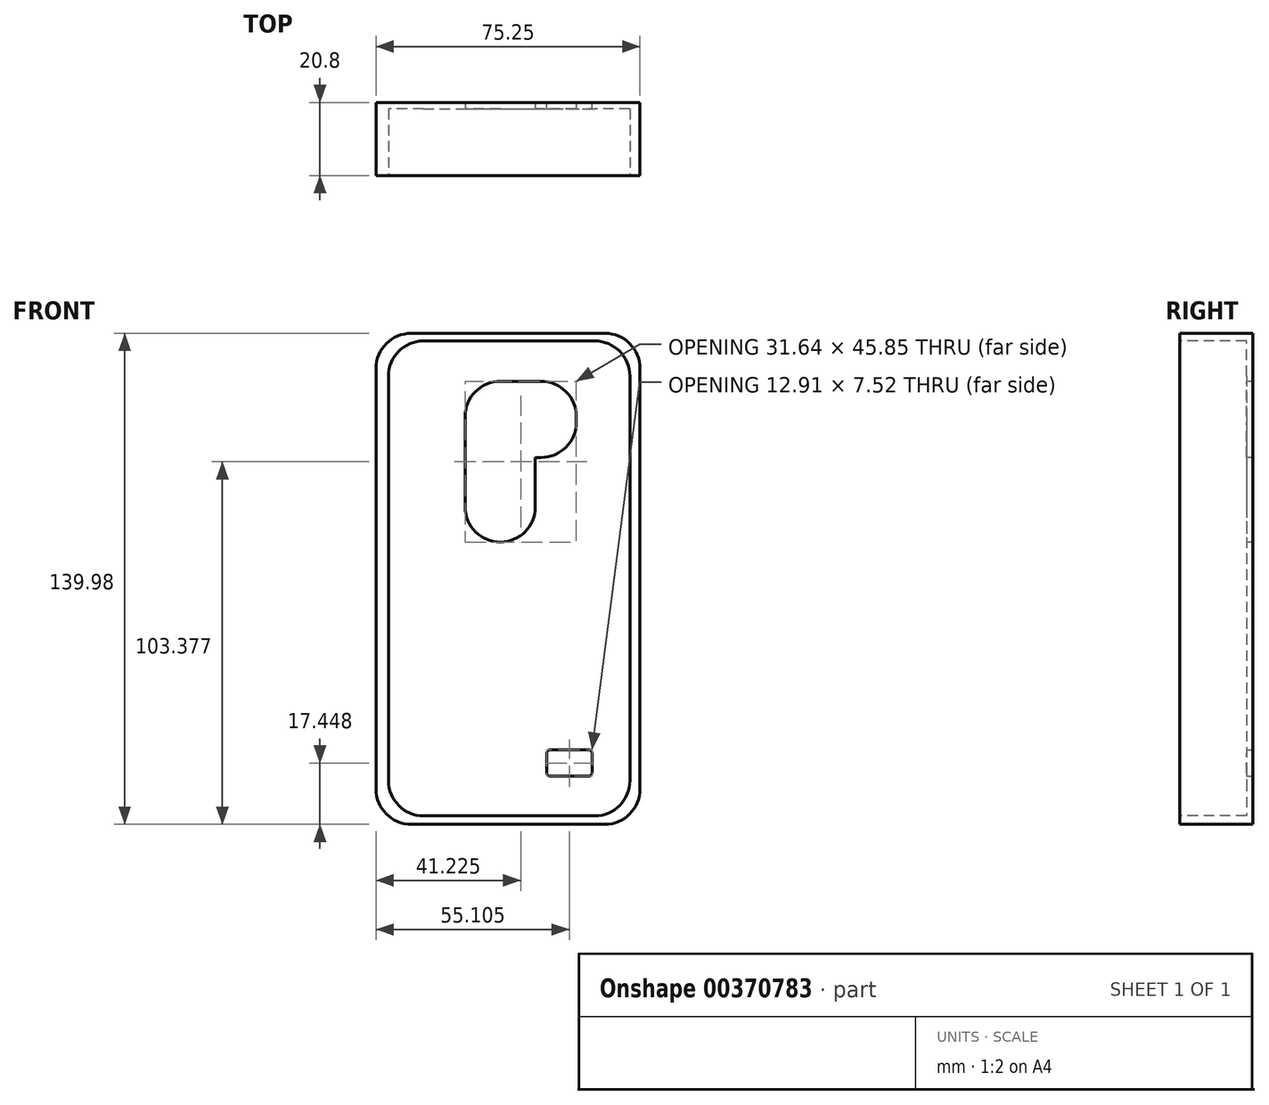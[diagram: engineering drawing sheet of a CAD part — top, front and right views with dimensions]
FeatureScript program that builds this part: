
annotation { "Feature Type Name" : "Feature", "Feature Type Description" : "" }
export const myFeature = defineFeature(function(context is Context, id is Id, definition is map)
    precondition{}
    {
        {
            var Q0;
            Q0=qCreatedBy(makeId("Front.planeOp"),FACE);
            var sketch = newSketch(context, id + "F0", { "sketchPlane" : qUnion([Q0])});
            skLineSegment(sketch, "E0.bottom", {"start": v(-27.78, 71) * mm, "end": v(27.47, 71) * mm});
            skLineSegment(sketch, "E0.top", {"start": v(-27.78, -68.98) * mm, "end": v(27.47, -68.98) * mm});
            skLineSegment(sketch, "E0.left", {"start": v(-37.78, 61) * mm, "end": v(-37.78, -58.98) * mm});
            skLineSegment(sketch, "E0.right", {"start": v(37.47, 61) * mm, "end": v(37.47, -58.98) * mm});
            skPoint(sketch, "E1.visualSharp", {"position": v(-37.78, 71) * mm});
            skArc(sketch, "E1.filletArc", {"start": v(-27.78, 71) * mm, "mid": v(-34.85, 68.07) * mm, "end": v(-37.78, 61) * mm});
            skPoint(sketch, "E2.visualSharp", {"position": v(37.47, 71) * mm});
            skArc(sketch, "E2.filletArc", {"start": v(37.47, 61) * mm, "mid": v(34.54, 68.07) * mm, "end": v(27.47, 71) * mm});
            skPoint(sketch, "E3.visualSharp", {"position": v(37.47, -68.98) * mm});
            skArc(sketch, "E3.filletArc", {"start": v(27.47, -68.98) * mm, "mid": v(34.54, -66.05) * mm, "end": v(37.47, -58.98) * mm});
            skPoint(sketch, "E4.visualSharp", {"position": v(-37.78, -68.98) * mm});
            skArc(sketch, "E4.filletArc", {"start": v(-37.78, -58.98) * mm, "mid": v(-34.85, -66.05) * mm, "end": v(-27.78, -68.98) * mm});
            skSolve(sketch);
        }
        {
            var Q0;
            Q0=makeQuery(id+"F0.imprint","IMPRINT",FACE,{"disambiguationData":[TD([[makeQuery(id+"F0.imprint","IMPRINT",EDGE,{"derivedFrom":sQuery(id+"F0.wireOp",EDGE,"E0.bottom")}),-1.0]])]});
            extrude(context, id + "F1", {"entities" : qUnion([Q0]), "depth" : 20.8 * mm});
        }
        {
            var Q0;
            Q0=makeQuery(id+"F1.opExtrude","CAP_FACE",FACE,{"disambiguationData":[OSD([sQuery(id+"F0.wireOp",EDGE,"E0.bottom"),sQuery(id+"F0.wireOp",EDGE,"E0.top"),sQuery(id+"F0.wireOp",EDGE,"E0.left"),sQuery(id+"F0.wireOp",EDGE,"E0.right"),sQuery(id+"F0.wireOp",EDGE,"E1.filletArc"),sQuery(id+"F0.wireOp",EDGE,"E2.filletArc"),sQuery(id+"F0.wireOp",EDGE,"E3.filletArc"),sQuery(id+"F0.wireOp",EDGE,"E4.filletArc")])],"isStart":false});
            var sketch = newSketch(context, id + "F2", { "sketchPlane" : qUnion([Q0])});
            skLineSegment(sketch, "E5.bottom", {"start": v(-24.27, 68.82) * mm, "end": v(24.58, 68.82) * mm});
            skLineSegment(sketch, "E5.top", {"start": v(-24.27, -66.56) * mm, "end": v(24.58, -66.56) * mm});
            skLineSegment(sketch, "E5.left", {"start": v(-34.27, 58.82) * mm, "end": v(-34.27, -56.56) * mm});
            skLineSegment(sketch, "E5.right", {"start": v(34.58, 58.82) * mm, "end": v(34.58, -56.56) * mm});
            skPoint(sketch, "E6.visualSharp", {"position": v(-34.27, 68.82) * mm});
            skArc(sketch, "E6.filletArc", {"start": v(-24.27, 68.82) * mm, "mid": v(-31.34, 65.9) * mm, "end": v(-34.27, 58.82) * mm});
            skPoint(sketch, "E7.visualSharp", {"position": v(34.58, 68.82) * mm});
            skArc(sketch, "E7.filletArc", {"start": v(34.58, 58.82) * mm, "mid": v(31.65, 65.9) * mm, "end": v(24.58, 68.82) * mm});
            skPoint(sketch, "E8.visualSharp", {"position": v(34.58, -66.56) * mm});
            skArc(sketch, "E8.filletArc", {"start": v(24.58, -66.56) * mm, "mid": v(31.65, -63.64) * mm, "end": v(34.58, -56.56) * mm});
            skPoint(sketch, "E9.visualSharp", {"position": v(-34.27, -66.56) * mm});
            skArc(sketch, "E9.filletArc", {"start": v(-34.27, -56.56) * mm, "mid": v(-31.34, -63.64) * mm, "end": v(-24.27, -66.56) * mm});
            skSolve(sketch);
        }
        {
            var Q0;
            Q0=makeQuery(id+"F2.imprint","IMPRINT",FACE,{"disambiguationData":[TD([[makeQuery(id+"F2.imprint","IMPRINT",EDGE,{"derivedFrom":sQuery(id+"F2.wireOp",EDGE,"E5.bottom")}),-1.0]])]});
            extrude(context, id + "F3", {"entities" : qUnion([Q0]), "operationType" : NewBodyOperationType.REMOVE, "oppositeDirection" : true, "depth" : 19 * mm});
        }
        {
            var Q0;
            Q0=makeQuery(id+"F3.boolean.opBoolean","COPY",FACE,{"derivedFrom":makeQuery(id+"F3.opExtrude","CAP_FACE",FACE,{"disambiguationData":[OSD([sQuery(id+"F2.wireOp",EDGE,"E5.bottom"),sQuery(id+"F2.wireOp",EDGE,"E5.top"),sQuery(id+"F2.wireOp",EDGE,"E5.left"),sQuery(id+"F2.wireOp",EDGE,"E5.right"),sQuery(id+"F2.wireOp",EDGE,"E6.filletArc"),sQuery(id+"F2.wireOp",EDGE,"E7.filletArc"),sQuery(id+"F2.wireOp",EDGE,"E8.filletArc"),sQuery(id+"F2.wireOp",EDGE,"E9.filletArc")])],"isStart":false})});
            var sketch = newSketch(context, id + "F4", { "sketchPlane" : qUnion([Q0])});
            skLineSegment(sketch, "E10.bottom", {"start": v(-2.37, 57.32) * mm, "end": v(9.27, 57.32) * mm});
            skLineSegment(sketch, "E10.left", {"start": v(-12.37, 47.32) * mm, "end": v(-12.37, 21.47) * mm});
            skLineSegment(sketch, "E11", {"start": v(9.27, 35.57) * mm, "end": v(7.63, 35.57) * mm});
            skLineSegment(sketch, "E12", {"start": v(7.63, 35.57) * mm, "end": v(7.63, 21.47) * mm});
            skLineSegment(sketch, "E13", {"start": v(19.27, 47.32) * mm, "end": v(19.27, 45.57) * mm});
            skLineSegment(sketch, "E14", {"start": v(-2.37, 11.47) * mm, "end": v(-2.37, 11.47) * mm});
            skPoint(sketch, "E15.visualSharp", {"position": v(19.27, 35.57) * mm});
            skArc(sketch, "E15.filletArc", {"start": v(9.27, 35.57) * mm, "mid": v(16.34, 38.5) * mm, "end": v(19.27, 45.57) * mm});
            skPoint(sketch, "E16.visualSharp", {"position": v(19.27, 57.32) * mm});
            skArc(sketch, "E16.filletArc", {"start": v(19.27, 47.32) * mm, "mid": v(16.34, 54.4) * mm, "end": v(9.27, 57.32) * mm});
            skPoint(sketch, "E17.visualSharp", {"position": v(-12.37, 57.32) * mm});
            skArc(sketch, "E17.filletArc", {"start": v(-2.37, 57.32) * mm, "mid": v(-9.45, 54.4) * mm, "end": v(-12.37, 47.32) * mm});
            skPoint(sketch, "E18.visualSharp", {"position": v(-12.37, 11.47) * mm});
            skArc(sketch, "E18.filletArc", {"start": v(-12.37, 21.47) * mm, "mid": v(-9.45, 14.4) * mm, "end": v(-2.37, 11.47) * mm});
            skPoint(sketch, "E19.visualSharp", {"position": v(7.63, 11.47) * mm});
            skArc(sketch, "E19.filletArc", {"start": v(-2.37, 11.47) * mm, "mid": v(4.7, 14.4) * mm, "end": v(7.63, 21.47) * mm});
            skSolve(sketch);
        }
        {
            var Q0;
            Q0=makeQuery(id+"F4.imprint","IMPRINT",FACE,{"disambiguationData":[TD([[makeQuery(id+"F4.imprint","IMPRINT",EDGE,{"derivedFrom":sQuery(id+"F4.wireOp",EDGE,"E10.bottom")}),-1.0]])]});
            extrude(context, id + "F5", {"entities" : qUnion([Q0]), "operationType" : NewBodyOperationType.REMOVE, "oppositeDirection" : true, "depth" : 25 * mm});
        }
        {
            var Q0;
            Q0=makeQuery(id+"F1.opExtrude","CAP_FACE",FACE,{"disambiguationData":[OSD([sQuery(id+"F0.wireOp",EDGE,"E0.bottom"),sQuery(id+"F0.wireOp",EDGE,"E0.top"),sQuery(id+"F0.wireOp",EDGE,"E0.left"),sQuery(id+"F0.wireOp",EDGE,"E0.right"),sQuery(id+"F0.wireOp",EDGE,"E1.filletArc"),sQuery(id+"F0.wireOp",EDGE,"E2.filletArc"),sQuery(id+"F0.wireOp",EDGE,"E3.filletArc"),sQuery(id+"F0.wireOp",EDGE,"E4.filletArc")])],"isStart":true});
            var sketch = newSketch(context, id + "F6", { "sketchPlane" : qUnion([Q0])});
            skLineSegment(sketch, "E20.bottom", {"start": v(-22.78, -47.77) * mm, "end": v(-11.87, -47.77) * mm});
            skLineSegment(sketch, "E20.top", {"start": v(-22.78, -55.3) * mm, "end": v(-11.87, -55.3) * mm});
            skLineSegment(sketch, "E20.left", {"start": v(-23.78, -48.77) * mm, "end": v(-23.78, -54.3) * mm});
            skLineSegment(sketch, "E20.right", {"start": v(-10.87, -48.77) * mm, "end": v(-10.87, -54.3) * mm});
            skPoint(sketch, "E21.visualSharp", {"position": v(-23.78, -47.77) * mm});
            skArc(sketch, "E21.filletArc", {"start": v(-22.78, -47.77) * mm, "mid": v(-23.49, -48.07) * mm, "end": v(-23.78, -48.77) * mm});
            skPoint(sketch, "E22.visualSharp", {"position": v(-10.87, -47.77) * mm});
            skArc(sketch, "E22.filletArc", {"start": v(-10.87, -48.77) * mm, "mid": v(-11.16, -48.07) * mm, "end": v(-11.87, -47.77) * mm});
            skPoint(sketch, "E23.visualSharp", {"position": v(-10.87, -55.3) * mm});
            skArc(sketch, "E23.filletArc", {"start": v(-11.87, -55.3) * mm, "mid": v(-11.16, -55) * mm, "end": v(-10.87, -54.3) * mm});
            skPoint(sketch, "E24.visualSharp", {"position": v(-23.78, -55.3) * mm});
            skArc(sketch, "E24.filletArc", {"start": v(-23.78, -54.3) * mm, "mid": v(-23.49, -55) * mm, "end": v(-22.78, -55.3) * mm});
            skSolve(sketch);
        }
        {
            var Q0;
            Q0=makeQuery(id+"F6.imprint","IMPRINT",FACE,{"disambiguationData":[TD([[makeQuery(id+"F6.imprint","IMPRINT",EDGE,{"derivedFrom":sQuery(id+"F6.wireOp",EDGE,"E20.bottom")}),-1.0]])]});
            extrude(context, id + "F7", {"entities" : qUnion([Q0]), "operationType" : NewBodyOperationType.REMOVE, "oppositeDirection" : true, "depth" : 25 * mm});
        }
    });
